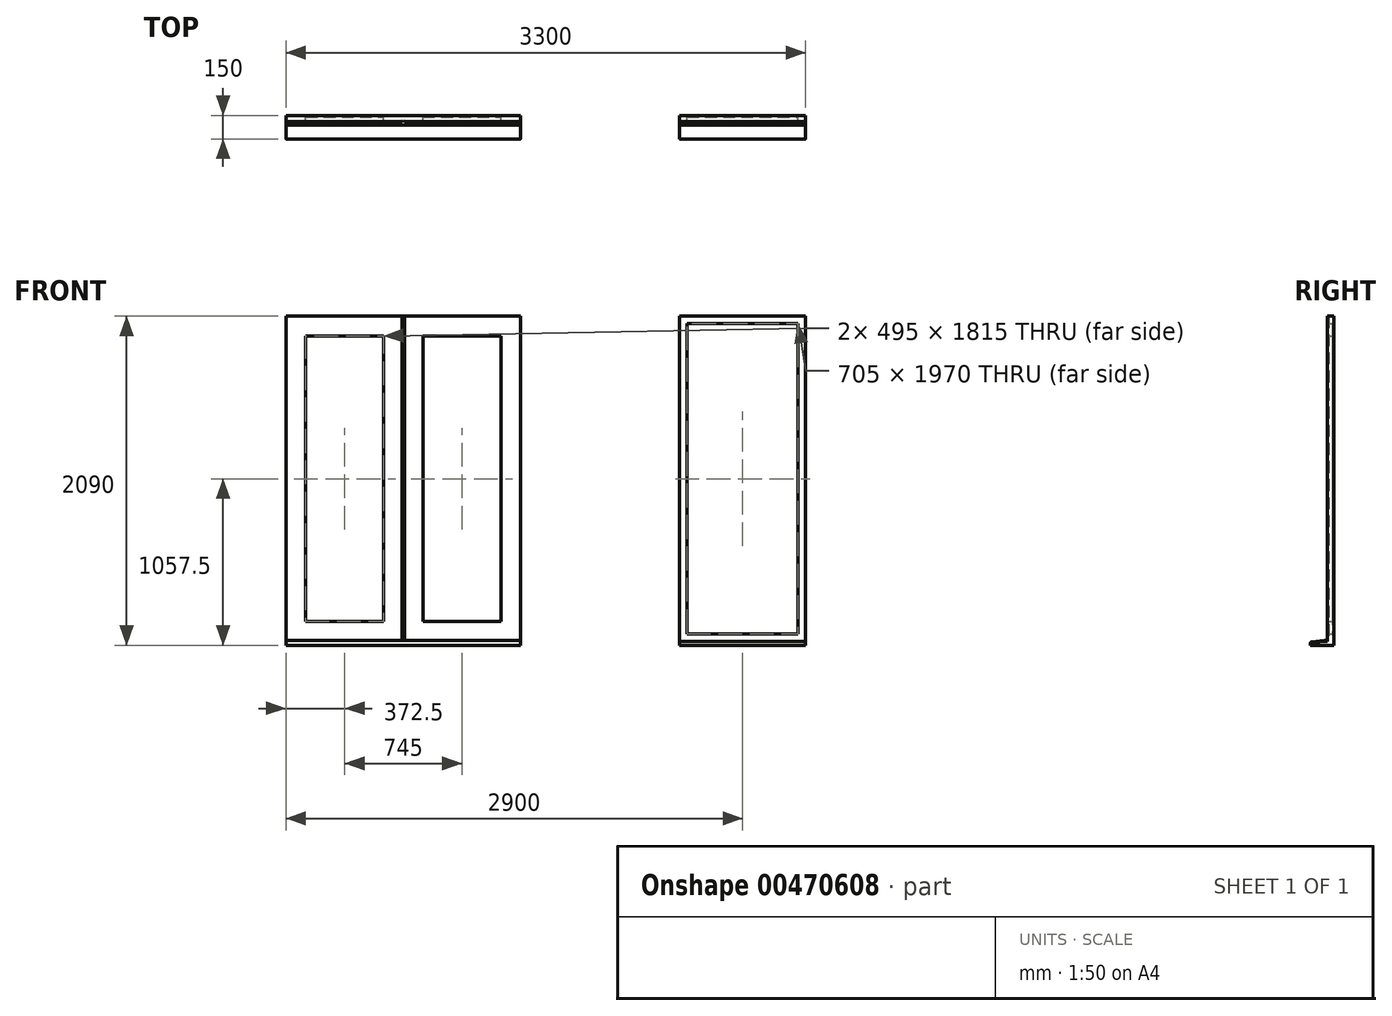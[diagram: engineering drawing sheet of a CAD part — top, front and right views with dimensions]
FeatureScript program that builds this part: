
annotation { "Feature Type Name" : "Feature", "Feature Type Description" : "" }
export const myFeature = defineFeature(function(context is Context, id is Id, definition is map)
    precondition{}
    {
        {
            var Q0;
            Q0=qCreatedBy(makeId("Front.planeOp"),FACE);
            var sketch = newSketch(context, id + "F0", { "sketchPlane" : qUnion([Q0])});
            skLineSegment(sketch, "E0.bottom", {"start": v(0, 0) * mm, "end": v(1490, 0) * mm});
            skLineSegment(sketch, "E0.top", {"start": v(0, 2090) * mm, "end": v(1490, 2090) * mm});
            skLineSegment(sketch, "E0.left", {"start": v(0, 0) * mm, "end": v(0, 2090) * mm});
            skLineSegment(sketch, "E0.right", {"start": v(1490, 0) * mm, "end": v(1490, 2090) * mm});
            skLineSegment(sketch, "E1", {"start": v(745, 2090) * mm, "end": v(745, 25) * mm});
            skLineSegment(sketch, "E2", {"start": v(0, 25) * mm, "end": v(1490, 25) * mm});
            skPoint(sketch, "E3.orphan", {"position": v(745, 0) * mm});
            skLineSegment(sketch, "E4.bottom", {"start": v(125, 1965) * mm, "end": v(620, 1965) * mm});
            skLineSegment(sketch, "E4.top", {"start": v(125, 150) * mm, "end": v(620, 150) * mm});
            skLineSegment(sketch, "E4.left", {"start": v(125, 1965) * mm, "end": v(125, 150) * mm});
            skLineSegment(sketch, "E4.right", {"start": v(620, 1965) * mm, "end": v(620, 150) * mm});
            skLineSegment(sketch, "E5.bottom", {"start": v(870, 1965) * mm, "end": v(1365, 1965) * mm});
            skLineSegment(sketch, "E5.top", {"start": v(870, 150) * mm, "end": v(1365, 150) * mm});
            skLineSegment(sketch, "E5.left", {"start": v(870, 1965) * mm, "end": v(870, 150) * mm});
            skLineSegment(sketch, "E5.right", {"start": v(1365, 1965) * mm, "end": v(1365, 150) * mm});
            skSolve(sketch);
        }
        {
            var Q0;
            Q0=qCreatedBy(makeId("Right.planeOp"),FACE);
            var sketch = newSketch(context, id + "F1", { "sketchPlane" : qUnion([Q0])});
            skLineSegment(sketch, "E6.bottom", {"start": v(0, 0) * mm, "end": v(-150, 0) * mm});
            skLineSegment(sketch, "E6.top", {"start": v(0, 30) * mm, "end": v(-150, 30) * mm});
            skLineSegment(sketch, "E6.left", {"start": v(0, 0) * mm, "end": v(0, 30) * mm});
            skLineSegment(sketch, "E6.right", {"start": v(-150, 0) * mm, "end": v(-150, 30) * mm});
            skSolve(sketch);
        }
        {
            var Q0;
            Q0=makeQuery(id+"F1.imprint","IMPRINT",FACE,{"disambiguationData":[TD([[makeQuery(id+"F1.imprint","IMPRINT",EDGE,{"derivedFrom":sQuery(id+"F1.wireOp",EDGE,"E6.bottom")}),-1.0]])]});
            extrude(context, id + "F2", {"entities" : qUnion([Q0]), "depth" : 1490 * mm});
        }
        {
            var Q0;
            Q0=makeQuery(id+"F2.opExtrude","SWEPT_EDGE",EDGE,{"disambiguationData":[OSD([sQuery(id+"F1.wireOp",EDGE,"E6.top"),sQuery(id+"F1.wireOp",EDGE,"E6.right")])]});
            chamfer(context, id + "F3", {"entities" : qUnion([Q0]), "chamferType" : ChamferType.TWO_OFFSETS, "width1" : 10 * mm, "oppositeDirection" : false, "width2" : 90 * mm, "tangentPropagation" : true});
        }
        {
            var Q0;
            {var subQ0=sQuery(id+"F1.wireOp",EDGE,"E6.right");Q0=makeQuery(id+"F3.opChamfer","BLEND_EDGE",EDGE,{"blendedFrom":[makeQuery(id+"F2.opExtrude","SWEPT_EDGE",EDGE,{"disambiguationData":[OSD([sQuery(id+"F1.wireOp",EDGE,"E6.top"),subQ0])]}),makeQuery(id+"F2.opExtrude","SWEPT_FACE",FACE,{"disambiguationData":[OSD([subQ0])]})],"blendedInto":[makeQuery(id+"F2.opExtrude","SWEPT_FACE",FACE,{"disambiguationData":[OSD([subQ0])]})]});}
            fillet(context, id + "F4", {"entities" : qUnion([Q0]), "radius" : 10 * mm, "tangentPropagation" : true, "allowEdgeOverflow" : false});
        }
        {
            var Q0;
            {var subQ1=sQuery(id+"F0.wireOp",EDGE,"E1");Q0=makeQuery(id+"F0.imprint","IMPRINT",FACE,{"disambiguationData":[TD([[makeQuery(id+"F0.imprint","IMPRINT",EDGE,{"derivedFrom":subQ1}),-1.0]])]});}
            extrude(context, id + "F5", {"entities" : qUnion([Q0]), "operationType" : NewBodyOperationType.ADD, "depth" : 40 * mm});
        }
        {
            var Q0;
            Q0=makeQuery(id+"F5.opExtrude","CAP_EDGE",EDGE,{"disambiguationData":[OSD([sQuery(id+"F0.wireOp",EDGE,"E1")])],"isStart":false});
            chamfer(context, id + "F6", {"entities" : qUnion([Q0]), "width" : 8 * mm, "tangentPropagation" : true});
        }
        {
            var Q0;
            {var subQ1=sQuery(id+"F0.wireOp",EDGE,"E1");Q0=makeQuery(id+"F0.imprint","IMPRINT",FACE,{"disambiguationData":[TD([[makeQuery(id+"F0.imprint","IMPRINT",EDGE,{"derivedFrom":subQ1}),1.0]])]});}
            extrude(context, id + "F7", {"entities" : qUnion([Q0]), "operationType" : NewBodyOperationType.ADD, "depth" : 40 * mm});
        }
        {
            var Q0;
            Q0=makeQuery(id+"F7.opExtrude","CAP_EDGE",EDGE,{"disambiguationData":[OSD([sQuery(id+"F0.wireOp",EDGE,"E1")])],"isStart":false});
            chamfer(context, id + "F8", {"entities" : qUnion([Q0]), "width" : 8 * mm, "tangentPropagation" : true});
        }
        {
            var Q0;
            Q0=makeQuery(id+"F0.imprint","IMPRINT",FACE,{"disambiguationData":[TD([[makeQuery(id+"F0.imprint","IMPRINT",EDGE,{"derivedFrom":sQuery(id+"F0.wireOp",EDGE,"E4.bottom")}),-1.0]])]});
            extrude(context, id + "F9", {"entities" : qUnion([Q0]), "depth" : 10 * mm});
        }
        {
            var Q0;
            Q0=makeQuery(id+"F0.imprint","IMPRINT",FACE,{"disambiguationData":[TD([[makeQuery(id+"F0.imprint","IMPRINT",EDGE,{"derivedFrom":sQuery(id+"F0.wireOp",EDGE,"E5.bottom")}),-1.0]])]});
            extrude(context, id + "F10", {"entities" : qUnion([Q0]), "depth" : 10 * mm});
        }
        {
            var Q0;
            Q0=qCreatedBy(makeId("Right.planeOp"),FACE);
            cPlane(context, id + "F11", {"entities" : qUnion([Q0]), "cplaneType" : CPlaneType.OFFSET, "offset" : 2500 * mm, "width" : 150 * mm, "height" : 150 * mm});
        }
        {
            var Q0;
            Q0=qCreatedBy(makeId("Front.planeOp"),FACE);
            var sketch = newSketch(context, id + "F12", { "sketchPlane" : qUnion([Q0])});
            skLineSegment(sketch, "E7.bottom", {"start": v(2500, 0) * mm, "end": v(3300, 0) * mm});
            skLineSegment(sketch, "E7.top", {"start": v(2500, 2090) * mm, "end": v(3300, 2090) * mm});
            skLineSegment(sketch, "E7.left", {"start": v(2500, 0) * mm, "end": v(2500, 2090) * mm});
            skLineSegment(sketch, "E7.right", {"start": v(3300, 0) * mm, "end": v(3300, 2090) * mm});
            skLineSegment(sketch, "E8", {"start": v(2500, 25) * mm, "end": v(3300, 25) * mm});
            skLineSegment(sketch, "E9.bottom", {"start": v(2547.5, 2042.5) * mm, "end": v(3252.5, 2042.5) * mm});
            skLineSegment(sketch, "E9.top", {"start": v(2547.5, 72.5) * mm, "end": v(3252.5, 72.5) * mm});
            skLineSegment(sketch, "E9.left", {"start": v(2547.5, 2042.5) * mm, "end": v(2547.5, 72.5) * mm});
            skLineSegment(sketch, "E9.right", {"start": v(3252.5, 2042.5) * mm, "end": v(3252.5, 72.5) * mm});
            skSolve(sketch);
        }
        {
            var Q0;
            Q0=qCreatedBy(id+"F11.planeOp",FACE);
            var sketch = newSketch(context, id + "F13", { "sketchPlane" : qUnion([Q0])});
            skLineSegment(sketch, "E10.bottom", {"start": v(0, 0) * mm, "end": v(-150, 0) * mm});
            skLineSegment(sketch, "E10.top", {"start": v(0, 25) * mm, "end": v(-150, 25) * mm});
            skLineSegment(sketch, "E10.left", {"start": v(0, 0) * mm, "end": v(0, 25) * mm});
            skLineSegment(sketch, "E10.right", {"start": v(-150, 0) * mm, "end": v(-150, 25) * mm});
            skSolve(sketch);
        }
        {
            var Q0;
            Q0 = qSketchRegion(id + "F13", true);
            extrude(context, id + "F14", {"entities" : qUnion([Q0]), "depth" : 800 * mm});
        }
        {
            var Q0;
            Q0=makeQuery(id+"F14.opExtrude","SWEPT_EDGE",EDGE,{"disambiguationData":[OSD([sQuery(id+"F13.wireOp",EDGE,"E10.top"),sQuery(id+"F13.wireOp",EDGE,"E10.right")])]});
            chamfer(context, id + "F15", {"entities" : qUnion([Q0]), "chamferType" : ChamferType.TWO_OFFSETS, "width1" : 10 * mm, "oppositeDirection" : false, "width2" : 90 * mm, "tangentPropagation" : true});
        }
        {
            var Q0;
            {var subQ0=sQuery(id+"F13.wireOp",EDGE,"E10.right");Q0=makeQuery(id+"F15.opChamfer","BLEND_EDGE",EDGE,{"blendedFrom":[makeQuery(id+"F14.opExtrude","SWEPT_EDGE",EDGE,{"disambiguationData":[OSD([sQuery(id+"F13.wireOp",EDGE,"E10.top"),subQ0])]}),makeQuery(id+"F14.opExtrude","SWEPT_FACE",FACE,{"disambiguationData":[OSD([subQ0])]})],"blendedInto":[makeQuery(id+"F14.opExtrude","SWEPT_FACE",FACE,{"disambiguationData":[OSD([subQ0])]})]});}
            fillet(context, id + "F16", {"entities" : qUnion([Q0]), "radius" : 10 * mm, "tangentPropagation" : true, "allowEdgeOverflow" : false});
        }
        {
            var Q0;
            {var subQ1=sQuery(id+"F12.wireOp",EDGE,"E7.top");Q0=makeQuery(id+"F12.imprint","IMPRINT",FACE,{"disambiguationData":[TD([[makeQuery(id+"F12.imprint","IMPRINT",EDGE,{"derivedFrom":subQ1}),-1.0]])]});}
            extrude(context, id + "F17", {"entities" : qUnion([Q0]), "operationType" : NewBodyOperationType.ADD, "depth" : 40 * mm});
        }
        {
            var Q0;
            Q0=makeQuery(id+"F12.imprint","IMPRINT",FACE,{"disambiguationData":[TD([[makeQuery(id+"F12.imprint","IMPRINT",EDGE,{"derivedFrom":sQuery(id+"F12.wireOp",EDGE,"E9.bottom")}),-1.0]])]});
            extrude(context, id + "F18", {"entities" : qUnion([Q0]), "depth" : 10 * mm});
        }
    });
